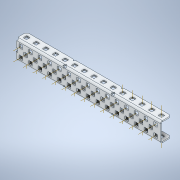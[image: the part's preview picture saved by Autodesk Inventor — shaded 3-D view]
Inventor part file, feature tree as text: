
AUTODESK INVENTOR PART (.ipt)
format: ipt  version: 2020 (Build 240168000, 168)  size: 1,251,840 bytes
history: native  units: in
note: dims shown in document units (in); Inventor stores cm internally (conversion verified against a paired STEP export)
features: other x68, plane x7, pattern_linear x4, split x1, sheet_metal_op x1
ambient origin geometry x8: Origin, YZ Plane, XZ Plane, XY Plane, X Axis, Y Axis, Z Axis, Center Point
bodies: Solid1 (feature_tree)
feature tree (81):
  other  "Work Axis1"
  pattern_linear  "Rectangular Pattern1"  Count1=15 Spacing1=0.5in
  other  "Work Axis72"
  pattern_linear  "Rectangular Pattern2"  Count1=15 Spacing1=0.5in
  pattern_linear  "Rectangular Pattern3"  Count1=5 Spacing1=0.5in
  other  "Work Axis141"
  pattern_linear  "Rectangular Pattern4"  Count1=14 Spacing1=0.5in
  plane  "Work Plane7"
  split  "Split1"
  plane  "Work Plane1"
  plane  "Work Plane2"
  other  "Work Point1"
  other  "Work Axis2"
  other  "Work Axis3"
  other  "Work Axis4"
  other  "Work Axis5"
  other  "Work Axis6"
  other  "Work Axis7"
  other  "Work Axis8"
  other  "Work Axis9"
  other  "Work Axis10"
  other  "Work Axis11"
  other  "Work Axis12"
  other  "Work Axis13"
  other  "Work Axis14"
  other  "Work Axis15"
  other  "Work Axis36"
  other  "Work Axis37"
  other  "Work Axis38"
  other  "Work Axis39"
  other  "Work Axis40"
  other  "Work Axis41"
  other  "Work Axis42"
  other  "Work Axis43"
  other  "Work Axis44"
  other  "Work Axis45"
  other  "Work Axis46"
  other  "Work Axis47"
  other  "Work Axis48"
  other  "Work Axis49"
  other  "Work Axis50"
  plane  "Work Plane3"
  plane  "Work Plane4"
  other  "Work Point2"
  other  "Work Axis71"
  other  "Work Point3"
  other  "Work Axis73"
  other  "Work Axis74"
  other  "Work Axis75"
  other  "Work Axis76"
  other  "Work Axis77"
  other  "Work Axis78"
  other  "Work Axis79"
  other  "Work Axis80"
  other  "Work Axis81"
  other  "Work Axis82"
  other  "Work Axis83"
  other  "Work Axis84"
  other  "Work Axis85"
  other  "Work Axis86"
  other  "Work Axis107"
  other  "Work Axis108"
  other  "Work Axis109"
  other  "Work Axis110"
  plane  "Work Plane5"
  plane  "Work Plane6"
  other  "Work Point4"
  other  "Work Axis142"
  other  "Work Axis143"
  other  "Work Axis144"
  other  "Work Axis145"
  other  "Work Axis146"
  other  "Work Axis147"
  other  "Work Axis148"
  other  "Work Axis149"
  other  "Work Axis150"
  other  "Work Axis151"
  other  "Work Axis152"
  other  "Work Axis153"
  other  "Work Axis154"
  sheet_metal_op  "Fold1"
